# Revit family: TY3388
name_source: partatom
category: Sprinklers
revit_build: Autodesk Revit 2016 (Build: 20150220_1215(x64)
units: mm (PartAtom-declared; Revit-internal decimal feet)

## family parameters
Always vertical = Yes
Cut with Voids When Loaded = No
Maintain Annotation Orientation = No
OmniClass Number = 23.65.70.17.11.24
OmniClass Title = Fire Fighting Sprinkler Heads
Part Type = Normal
Room Calculation Point = No
Round Connector Dimension = Use Diameter
Shared = No
Work Plane-Based = No

## types (8) — shared parameters
COBie = Yes
COBie.Component.Name = Sprinklers:Window Horiz Sidewall_SIN
COBie.Type = Yes
COBie.Type.AssetType = Fixed
COBie.Type.Category = Pr_70_55_97_84:Sprinklers
COBie.Type.DurationUnit = year
COBie.Type.Manufacturer = Tyco Fire Protection Products
COBie.Type.Material = Brass
COBie.Type.NominalHeight = 0' - 0"
COBie.Type.NominalLength = 0' - 0"
COBie.Type.NominalWidth = 0' - 0"
COBie.Type.Shape = Cylinder
COBie.Type.Size = 1/2"(DN15)
COBie.Type.WarrantyGuarantorParts = http://tycofsbp.com
Coverage = Standard
K-Factor = 5.5493
Manufacturer = Tyco Fire Protection Products
Manufacturer URL = www.tyco-fire.com
Model = WS
Nominal Diameter 1 = 1"
Orifice = Standard
Orifice Size = 0"
Outside Diameter 1 = 1"
Response = Quick
SIN No = TY3388
Takeout 1 = 2"
Technical Data Sheet No = TFP620
zero-valued in all types: COBie.Type.ReplacementCost, Style Id

## per-type parameters (varying)
| type | COBie.Component.Description | COBie.Type.Colour | COBie.Type.Finish | COBie.Type.ModelNumber | COBie.Type.ModelReference | Part No | Temperature Rating |
| WS Wet Window Horiz Sidewall_Yellow_155   68.3°C K80 DN15 NPT Br_50-305-1-155 | WS Wet Window Horiz Sidewall  68.3°C K80 DN15 NPT Br | Yellow | Natural Brass | 50-305-1-155 | WS Wet Window Horiz Sidewall  68.3°C K80 DN15 NPT Br | 50-305-1-155 | 155 °F |
| WS Wet Window Horiz Sidewall_Yellow_200  93.3°C K80 DN15 NPT Br_50-305-1-200 | WS Wet Window Horiz Sidewall  93.3°C K80 DN15 NPT Br | Yellow | Natural Brass | 50-305-1-200 | WS Wet Window Horiz Sidewall  93.3°C K80 DN15 NPT Br | 50-305-1-200 | 200 °F |
| WS Wet Window Horiz Sidewall_White_155   68.3°C K80 DN15 NPT Wh9003_50-305-4-155 | WS Wet Window Horiz Sidewall  68.3°C K80 DN15 NPT Wh9003 | White | Signal White | 50-305-4-155 | WS Wet Window Horiz Sidewall  68.3°C K80 DN15 NPT Wh9003 | 50-305-4-155 | 155 °F |
| WS Wet Window Horiz Sidewall_White_200  93.3°C K80 DN15 NPT Wh9003_50-305-4-200 | WS Wet Window Horiz Sidewall  93.3°C K80 DN15 NPT Wh9003 | White | Signal White | 50-305-4-200 | WS Wet Window Horiz Sidewall  93.3°C K80 DN15 NPT Wh9003 | 50-305-4-200 | 200 °F |
| WS Wet Window Horiz Sidewall_Black_155  68.3°C K80 DN15 NPT Wh9003_50-305-5-155 | WS Wet Window Horiz Sidewall_White_155   68.3°C K80 DN15 NPT Wh9003 | Black | Jet Black | 50-305-5-155 | WS Wet Window Horiz Sidewall_White_155   68.3°C K80 DN15 NPT Wh9003 | 50-305-5-155 | 155 °F |
| WS Wet Window Horiz Sidewall_Black_200  93.3°C K80 DN15 NPT Wh9003_50-305-5-200 | WS Wet Window Horiz Sidewall_White_200  93.3°C K80 DN15 NPT Wh9003 | Black | Jet Black | 50-305-5-200 | WS Wet Window Horiz Sidewall_White_200  93.3°C K80 DN15 NPT Wh9003 | 50-305-5-200 | 200 °F |
| WS Wet Window Horiz Sidewall_Silver_155  68.3°C K80 DN15 NPT Chr_50-305-9-155 | WS Wet Window Horiz Sidewall  68.3°C K80 DN15 NPT Chr | Silver | Chrome Plated | 50-305-9-155 | WS Wet Window Horiz Sidewall  68.3°C K80 DN15 NPT Chr | 50-305-9-155 | 155 °F |
| WS Wet Window Horiz Sidewall_Silver_200  93.3°C K80 DN15 NPT Chr_50-305-9-200 | WS Wet Window Horiz Sidewall  93.3°C K80 DN15 NPT Chr | Silver | Chrome Plated | 50-305-9-200 | WS Wet Window Horiz Sidewall  93.3°C K80 DN15 NPT Chr | 50-305-9-200 | 200 °F |

note: column(s) folded — value = type name in every type: Description

## geometry (parser evidence)
native form markers: Blend x4, Sweep x50
no freeform markers — native parametric forms only
